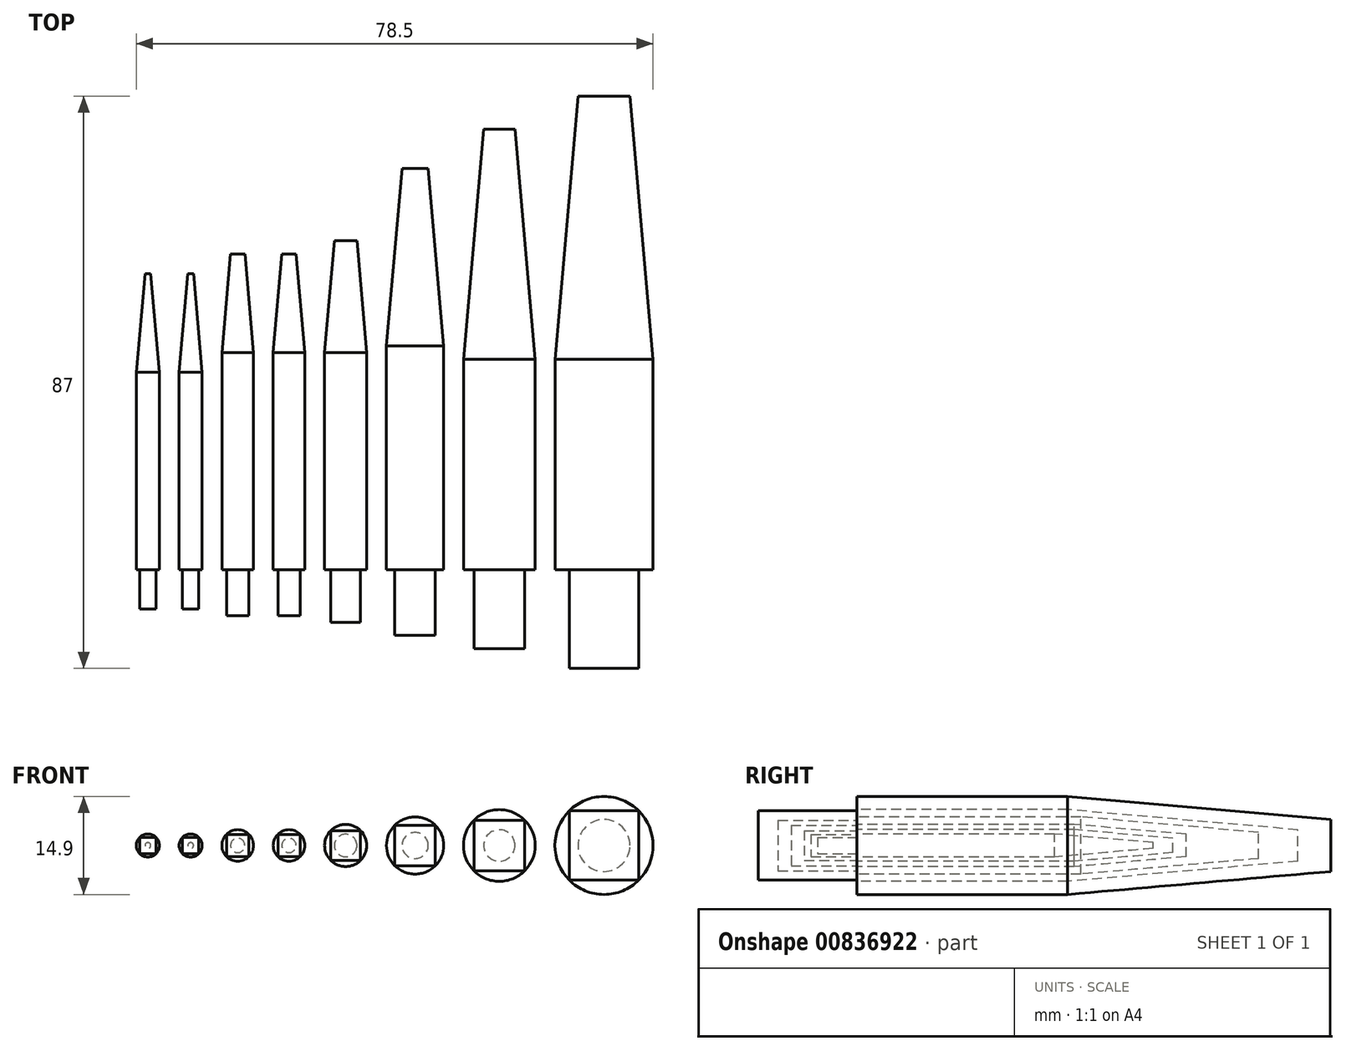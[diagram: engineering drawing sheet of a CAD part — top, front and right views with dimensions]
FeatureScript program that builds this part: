
annotation { "Feature Type Name" : "Feature", "Feature Type Description" : "" }
export const myFeature = defineFeature(function(context is Context, id is Id, definition is map)
    precondition{}
    {
        {
            var Q0;
            Q0=qCreatedBy(makeId("Front.planeOp"),FACE);
            var sketch = newSketch(context, id + "F0", { "sketchPlane" : qUnion([Q0])});
            skCircle(sketch, "E0", {"center": v(-27.49, 0) * mm, "radius": 2.4 * mm});
            skCircle(sketch, "E1", {"center": v(-19.69, 0) * mm, "radius": 2.4 * mm});
            skCircle(sketch, "E2", {"center": v(-11.09, 0) * mm, "radius": 3.2 * mm});
            skCircle(sketch, "E3", {"center": v(-0.54, 0) * mm, "radius": 4.35 * mm});
            skCircle(sketch, "E4", {"center": v(12.26, 0) * mm, "radius": 5.45 * mm});
            skCircle(sketch, "E5", {"center": v(28.16, 0) * mm, "radius": 7.45 * mm});
            skCircle(sketch, "E6", {"center": v(-34.64, 0) * mm, "radius": 1.75 * mm});
            skCircle(sketch, "E7", {"center": v(-41.14, 0) * mm, "radius": 1.75 * mm});
            skLineSegment(sketch, "E8.bottom", {"start": v(-42.37, 1.24) * mm, "end": v(-39.9, 1.24) * mm});
            skLineSegment(sketch, "E8.top", {"start": v(-42.37, -1.24) * mm, "end": v(-39.9, -1.24) * mm});
            skLineSegment(sketch, "E8.left", {"start": v(-42.37, 1.24) * mm, "end": v(-42.37, -1.24) * mm});
            skLineSegment(sketch, "E8.right", {"start": v(-39.9, 1.24) * mm, "end": v(-39.9, -1.24) * mm});
            skLineSegment(sketch, "E9.bottom", {"start": v(-35.87, 1.24) * mm, "end": v(-33.4, 1.24) * mm});
            skLineSegment(sketch, "E9.top", {"start": v(-35.87, -1.24) * mm, "end": v(-33.4, -1.24) * mm});
            skLineSegment(sketch, "E9.left", {"start": v(-35.87, 1.24) * mm, "end": v(-35.87, -1.24) * mm});
            skLineSegment(sketch, "E9.right", {"start": v(-33.4, 1.24) * mm, "end": v(-33.4, -1.24) * mm});
            skLineSegment(sketch, "E10.bottom", {"start": v(-29.18, 1.7) * mm, "end": v(-25.79, 1.7) * mm});
            skLineSegment(sketch, "E10.top", {"start": v(-29.18, -1.7) * mm, "end": v(-25.79, -1.7) * mm});
            skLineSegment(sketch, "E10.left", {"start": v(-29.18, 1.7) * mm, "end": v(-29.18, -1.7) * mm});
            skLineSegment(sketch, "E10.right", {"start": v(-25.79, 1.7) * mm, "end": v(-25.79, -1.7) * mm});
            skLineSegment(sketch, "E11.bottom", {"start": v(-21.38, 1.7) * mm, "end": v(-17.99, 1.7) * mm});
            skLineSegment(sketch, "E11.top", {"start": v(-21.38, -1.7) * mm, "end": v(-17.99, -1.7) * mm});
            skLineSegment(sketch, "E11.left", {"start": v(-21.38, 1.7) * mm, "end": v(-21.38, -1.7) * mm});
            skLineSegment(sketch, "E11.right", {"start": v(-17.99, 1.7) * mm, "end": v(-17.99, -1.7) * mm});
            skLineSegment(sketch, "E12.bottom", {"start": v(-13.35, 2.26) * mm, "end": v(-8.82, 2.26) * mm});
            skLineSegment(sketch, "E12.top", {"start": v(-13.35, -2.26) * mm, "end": v(-8.82, -2.26) * mm});
            skLineSegment(sketch, "E12.left", {"start": v(-13.35, 2.26) * mm, "end": v(-13.35, -2.26) * mm});
            skLineSegment(sketch, "E12.right", {"start": v(-8.82, 2.26) * mm, "end": v(-8.82, -2.26) * mm});
            skLineSegment(sketch, "E13.bottom", {"start": v(-3.61, 3.08) * mm, "end": v(2.54, 3.08) * mm});
            skLineSegment(sketch, "E13.top", {"start": v(-3.61, -3.08) * mm, "end": v(2.54, -3.08) * mm});
            skLineSegment(sketch, "E13.left", {"start": v(-3.61, 3.08) * mm, "end": v(-3.61, -3.08) * mm});
            skLineSegment(sketch, "E13.right", {"start": v(2.54, 3.08) * mm, "end": v(2.54, -3.08) * mm});
            skLineSegment(sketch, "E14.bottom", {"start": v(8.4, 3.85) * mm, "end": v(16.12, 3.85) * mm});
            skLineSegment(sketch, "E14.top", {"start": v(8.4, -3.85) * mm, "end": v(16.12, -3.85) * mm});
            skLineSegment(sketch, "E14.left", {"start": v(8.4, 3.85) * mm, "end": v(8.4, -3.85) * mm});
            skLineSegment(sketch, "E14.right", {"start": v(16.12, 3.85) * mm, "end": v(16.12, -3.85) * mm});
            skLineSegment(sketch, "E15.bottom", {"start": v(22.9, 5.27) * mm, "end": v(33.43, 5.27) * mm});
            skLineSegment(sketch, "E15.top", {"start": v(22.9, -5.27) * mm, "end": v(33.43, -5.27) * mm});
            skLineSegment(sketch, "E15.left", {"start": v(22.9, 5.27) * mm, "end": v(22.9, -5.27) * mm});
            skLineSegment(sketch, "E15.right", {"start": v(33.43, 5.27) * mm, "end": v(33.43, -5.27) * mm});
            skSolve(sketch);
        }
        {
            var Q0;
            Q0=makeQuery(id+"F0.imprint","IMPRINT",FACE,{"disambiguationData":[TD([[makeQuery(id+"F0.imprint","IMPRINT",EDGE,{"derivedFrom":sQuery(id+"F0.wireOp",EDGE,"E7")}),1.0]])]});
            var Q1;
            Q1=makeQuery(id+"F0.imprint","IMPRINT",FACE,{"disambiguationData":[TD([[makeQuery(id+"F0.imprint","IMPRINT",EDGE,{"derivedFrom":sQuery(id+"F0.wireOp",EDGE,"E6")}),1.0]])]});
            var Q2;
            Q2=makeQuery(id+"F0.imprint","IMPRINT",FACE,{"disambiguationData":[TD([[makeQuery(id+"F0.imprint","IMPRINT",EDGE,{"derivedFrom":sQuery(id+"F0.wireOp",EDGE,"E8.bottom")}),-1.0]])]});
            var Q3;
            Q3=makeQuery(id+"F0.imprint","IMPRINT",FACE,{"disambiguationData":[TD([[makeQuery(id+"F0.imprint","IMPRINT",EDGE,{"derivedFrom":sQuery(id+"F0.wireOp",EDGE,"E9.bottom")}),-1.0]])]});
            extrude(context, id + "F1", {"entities" : qUnion([Q0, Q1, Q2, Q3]), "oppositeDirection" : true, "depth" : 30 * mm, "offsetDistance" : 25 * mm});
        }
        {
            var Q0;
            Q0=makeQuery(id+"F0.imprint","IMPRINT",FACE,{"disambiguationData":[TD([[makeQuery(id+"F0.imprint","IMPRINT",EDGE,{"derivedFrom":sQuery(id+"F0.wireOp",EDGE,"E0")}),1.0]])]});
            var Q1;
            Q1=makeQuery(id+"F0.imprint","IMPRINT",FACE,{"disambiguationData":[TD([[makeQuery(id+"F0.imprint","IMPRINT",EDGE,{"derivedFrom":sQuery(id+"F0.wireOp",EDGE,"E1")}),1.0]])]});
            var Q2;
            Q2=makeQuery(id+"F0.imprint","IMPRINT",FACE,{"disambiguationData":[TD([[makeQuery(id+"F0.imprint","IMPRINT",EDGE,{"derivedFrom":sQuery(id+"F0.wireOp",EDGE,"E2")}),1.0]])]});
            var Q3;
            Q3=makeQuery(id+"F0.imprint","IMPRINT",FACE,{"disambiguationData":[TD([[makeQuery(id+"F0.imprint","IMPRINT",EDGE,{"derivedFrom":sQuery(id+"F0.wireOp",EDGE,"E10.bottom")}),-1.0]])]});
            var Q4;
            Q4=makeQuery(id+"F0.imprint","IMPRINT",FACE,{"disambiguationData":[TD([[makeQuery(id+"F0.imprint","IMPRINT",EDGE,{"derivedFrom":sQuery(id+"F0.wireOp",EDGE,"E11.bottom")}),-1.0]])]});
            var Q5;
            Q5=makeQuery(id+"F0.imprint","IMPRINT",FACE,{"disambiguationData":[TD([[makeQuery(id+"F0.imprint","IMPRINT",EDGE,{"derivedFrom":sQuery(id+"F0.wireOp",EDGE,"E12.bottom")}),-1.0]])]});
            extrude(context, id + "F2", {"entities" : qUnion([Q0, Q1, Q2, Q3, Q4, Q5]), "oppositeDirection" : true, "depth" : 33 * mm, "offsetDistance" : 25 * mm});
        }
        {
            var Q0;
            Q0=makeQuery(id+"F0.imprint","IMPRINT",FACE,{"disambiguationData":[TD([[makeQuery(id+"F0.imprint","IMPRINT",EDGE,{"derivedFrom":sQuery(id+"F0.wireOp",EDGE,"E3")}),1.0]])]});
            var Q1;
            Q1=makeQuery(id+"F0.imprint","IMPRINT",FACE,{"disambiguationData":[TD([[makeQuery(id+"F0.imprint","IMPRINT",EDGE,{"derivedFrom":sQuery(id+"F0.wireOp",EDGE,"E13.bottom")}),-1.0]])]});
            extrude(context, id + "F3", {"entities" : qUnion([Q0, Q1]), "oppositeDirection" : true, "depth" : 34 * mm, "offsetDistance" : 25 * mm});
        }
        {
            var Q0;
            Q0=makeQuery(id+"F0.imprint","IMPRINT",FACE,{"disambiguationData":[TD([[makeQuery(id+"F0.imprint","IMPRINT",EDGE,{"derivedFrom":sQuery(id+"F0.wireOp",EDGE,"E4")}),1.0]])]});
            var Q1;
            Q1=makeQuery(id+"F0.imprint","IMPRINT",FACE,{"disambiguationData":[TD([[makeQuery(id+"F0.imprint","IMPRINT",EDGE,{"derivedFrom":sQuery(id+"F0.wireOp",EDGE,"E5")}),1.0]])]});
            var Q2;
            Q2=makeQuery(id+"F0.imprint","IMPRINT",FACE,{"disambiguationData":[TD([[makeQuery(id+"F0.imprint","IMPRINT",EDGE,{"derivedFrom":sQuery(id+"F0.wireOp",EDGE,"E14.bottom")}),-1.0]])]});
            var Q3;
            Q3=makeQuery(id+"F0.imprint","IMPRINT",FACE,{"disambiguationData":[TD([[makeQuery(id+"F0.imprint","IMPRINT",EDGE,{"derivedFrom":sQuery(id+"F0.wireOp",EDGE,"E15.bottom")}),-1.0]])]});
            extrude(context, id + "F4", {"entities" : qUnion([Q0, Q1, Q2, Q3]), "oppositeDirection" : true, "depth" : 32 * mm, "offsetDistance" : 25 * mm});
        }
        {
            var Q0;
            Q0=makeQuery(id+"F0.imprint","IMPRINT",FACE,{"disambiguationData":[TD([[makeQuery(id+"F0.imprint","IMPRINT",EDGE,{"derivedFrom":sQuery(id+"F0.wireOp",EDGE,"E8.bottom")}),-1.0]])]});
            var Q1;
            Q1=makeQuery(id+"F0.imprint","IMPRINT",FACE,{"disambiguationData":[TD([[makeQuery(id+"F0.imprint","IMPRINT",EDGE,{"derivedFrom":sQuery(id+"F0.wireOp",EDGE,"E9.bottom")}),-1.0]])]});
            extrude(context, id + "F5", {"entities" : qUnion([Q0, Q1]), "depth" : 6 * mm, "offsetDistance" : 25 * mm});
        }
        {
            var Q0;
            Q0=makeQuery(id+"F0.imprint","IMPRINT",FACE,{"disambiguationData":[TD([[makeQuery(id+"F0.imprint","IMPRINT",EDGE,{"derivedFrom":sQuery(id+"F0.wireOp",EDGE,"E10.bottom")}),-1.0]])]});
            var Q1;
            Q1=makeQuery(id+"F0.imprint","IMPRINT",FACE,{"disambiguationData":[TD([[makeQuery(id+"F0.imprint","IMPRINT",EDGE,{"derivedFrom":sQuery(id+"F0.wireOp",EDGE,"E11.bottom")}),-1.0]])]});
            extrude(context, id + "F6", {"entities" : qUnion([Q0, Q1]), "depth" : 7 * mm, "offsetDistance" : 25 * mm});
        }
        {
            var Q0;
            Q0=makeQuery(id+"F0.imprint","IMPRINT",FACE,{"disambiguationData":[TD([[makeQuery(id+"F0.imprint","IMPRINT",EDGE,{"derivedFrom":sQuery(id+"F0.wireOp",EDGE,"E12.bottom")}),-1.0]])]});
            extrude(context, id + "F7", {"entities" : qUnion([Q0]), "operationType" : NewBodyOperationType.ADD, "depth" : 8 * mm, "offsetDistance" : 25 * mm});
        }
        {
            var Q0;
            Q0=makeQuery(id+"F0.imprint","IMPRINT",FACE,{"disambiguationData":[TD([[makeQuery(id+"F0.imprint","IMPRINT",EDGE,{"derivedFrom":sQuery(id+"F0.wireOp",EDGE,"E13.bottom")}),-1.0]])]});
            extrude(context, id + "F8", {"entities" : qUnion([Q0]), "operationType" : NewBodyOperationType.ADD, "depth" : 10 * mm, "offsetDistance" : 25 * mm});
        }
        {
            var Q0;
            Q0=makeQuery(id+"F0.imprint","IMPRINT",FACE,{"disambiguationData":[TD([[makeQuery(id+"F0.imprint","IMPRINT",EDGE,{"derivedFrom":sQuery(id+"F0.wireOp",EDGE,"E14.bottom")}),-1.0]])]});
            extrude(context, id + "F9", {"entities" : qUnion([Q0]), "operationType" : NewBodyOperationType.ADD, "depth" : 12 * mm, "offsetDistance" : 25 * mm});
        }
        {
            var Q0;
            Q0=makeQuery(id+"F0.imprint","IMPRINT",FACE,{"disambiguationData":[TD([[makeQuery(id+"F0.imprint","IMPRINT",EDGE,{"derivedFrom":sQuery(id+"F0.wireOp",EDGE,"E15.bottom")}),-1.0]])]});
            extrude(context, id + "F10", {"entities" : qUnion([Q0]), "operationType" : NewBodyOperationType.ADD, "depth" : 15 * mm, "offsetDistance" : 25 * mm});
        }
        {
            var Q0;
            Q0=makeQuery(id+"F4.opExtrude","CAP_FACE",FACE,{"disambiguationData":[OSD([sQuery(id+"F0.wireOp",EDGE,"E5")])],"isStart":false});
            extrude(context, id + "F11", {"entities" : qUnion([Q0]), "operationType" : NewBodyOperationType.ADD, "depth" : 40 * mm, "offsetDistance" : 25 * mm});
        }
        {
            var Q0;
            Q0=makeQuery(id+"F11.opExtrude","CAP_EDGE",EDGE,{"disambiguationData":[OSD([sQuery(id+"F0.wireOp",EDGE,"E5")])],"isStart":false});
            chamfer(context, id + "F12", {"entities" : qUnion([Q0]), "chamferType" : ChamferType.OFFSET_ANGLE, "width" : 40 * mm, "oppositeDirection" : false, "angle" : 5 * degree, "tangentPropagation" : true});
        }
        {
            var Q0;
            Q0=makeQuery(id+"F4.opExtrude","CAP_FACE",FACE,{"disambiguationData":[OSD([sQuery(id+"F0.wireOp",EDGE,"E4")])],"isStart":false});
            extrude(context, id + "F13", {"entities" : qUnion([Q0]), "operationType" : NewBodyOperationType.ADD, "depth" : 35 * mm, "offsetDistance" : 25 * mm});
        }
        {
            var Q0;
            Q0=makeQuery(id+"F13.opExtrude","CAP_EDGE",EDGE,{"disambiguationData":[OSD([sQuery(id+"F0.wireOp",EDGE,"E4")])],"isStart":false});
            chamfer(context, id + "F14", {"entities" : qUnion([Q0]), "chamferType" : ChamferType.OFFSET_ANGLE, "width" : 35 * mm, "oppositeDirection" : false, "angle" : 5 * degree, "tangentPropagation" : true});
        }
        {
            var Q0;
            Q0=makeQuery(id+"F3.opExtrude","CAP_FACE",FACE,{"disambiguationData":[OSD([sQuery(id+"F0.wireOp",EDGE,"E3")])],"isStart":false});
            extrude(context, id + "F15", {"entities" : qUnion([Q0]), "operationType" : NewBodyOperationType.ADD, "depth" : 27 * mm, "offsetDistance" : 25 * mm});
        }
        {
            var Q0;
            Q0=makeQuery(id+"F15.opExtrude","CAP_EDGE",EDGE,{"disambiguationData":[OSD([sQuery(id+"F0.wireOp",EDGE,"E3")])],"isStart":false});
            chamfer(context, id + "F16", {"entities" : qUnion([Q0]), "chamferType" : ChamferType.OFFSET_ANGLE, "width" : 27 * mm, "oppositeDirection" : false, "angle" : 5 * degree, "tangentPropagation" : true});
        }
        {
            var Q0;
            Q0=makeQuery(id+"F2.opExtrude","CAP_FACE",FACE,{"disambiguationData":[OSD([sQuery(id+"F0.wireOp",EDGE,"E2")])],"isStart":false});
            extrude(context, id + "F17", {"entities" : qUnion([Q0]), "operationType" : NewBodyOperationType.ADD, "depth" : 17 * mm, "offsetDistance" : 25 * mm});
        }
        {
            var Q0;
            Q0=makeQuery(id+"F17.opExtrude","CAP_EDGE",EDGE,{"disambiguationData":[OSD([sQuery(id+"F0.wireOp",EDGE,"E2")])],"isStart":false});
            chamfer(context, id + "F18", {"entities" : qUnion([Q0]), "chamferType" : ChamferType.OFFSET_ANGLE, "width" : 17 * mm, "oppositeDirection" : false, "angle" : 5 * degree, "tangentPropagation" : true});
        }
        {
            var Q0;
            Q0=makeQuery(id+"F2.opExtrude","CAP_FACE",FACE,{"disambiguationData":[OSD([sQuery(id+"F0.wireOp",EDGE,"E1")])],"isStart":false});
            var Q1;
            Q1=makeQuery(id+"F2.opExtrude","CAP_FACE",FACE,{"disambiguationData":[OSD([sQuery(id+"F0.wireOp",EDGE,"E0")])],"isStart":false});
            var Q2;
            Q2=makeQuery(id+"F1.opExtrude","CAP_FACE",FACE,{"disambiguationData":[OSD([sQuery(id+"F0.wireOp",EDGE,"E6")])],"isStart":false});
            var Q3;
            Q3=makeQuery(id+"F1.opExtrude","CAP_FACE",FACE,{"disambiguationData":[OSD([sQuery(id+"F0.wireOp",EDGE,"E7")])],"isStart":false});
            extrude(context, id + "F19", {"entities" : qUnion([Q0, Q1, Q2, Q3]), "depth" : 15 * mm, "offsetDistance" : 25 * mm});
        }
        {
            var Q0;
            Q0=makeQuery(id+"F19.opExtrude","CAP_EDGE",EDGE,{"disambiguationData":[OSD([sQuery(id+"F0.wireOp",EDGE,"E1")])],"isStart":false});
            var Q1;
            Q1=makeQuery(id+"F19.opExtrude","CAP_EDGE",EDGE,{"disambiguationData":[OSD([sQuery(id+"F0.wireOp",EDGE,"E0")])],"isStart":false});
            var Q2;
            Q2=makeQuery(id+"F19.opExtrude","CAP_EDGE",EDGE,{"disambiguationData":[OSD([sQuery(id+"F0.wireOp",EDGE,"E6")])],"isStart":false});
            var Q3;
            Q3=makeQuery(id+"F19.opExtrude","CAP_EDGE",EDGE,{"disambiguationData":[OSD([sQuery(id+"F0.wireOp",EDGE,"E7")])],"isStart":false});
            chamfer(context, id + "F20", {"entities" : qUnion([Q0, Q1, Q2, Q3]), "chamferType" : ChamferType.OFFSET_ANGLE, "width" : 15 * mm, "oppositeDirection" : false, "angle" : 5 * degree, "tangentPropagation" : true});
        }
    });
